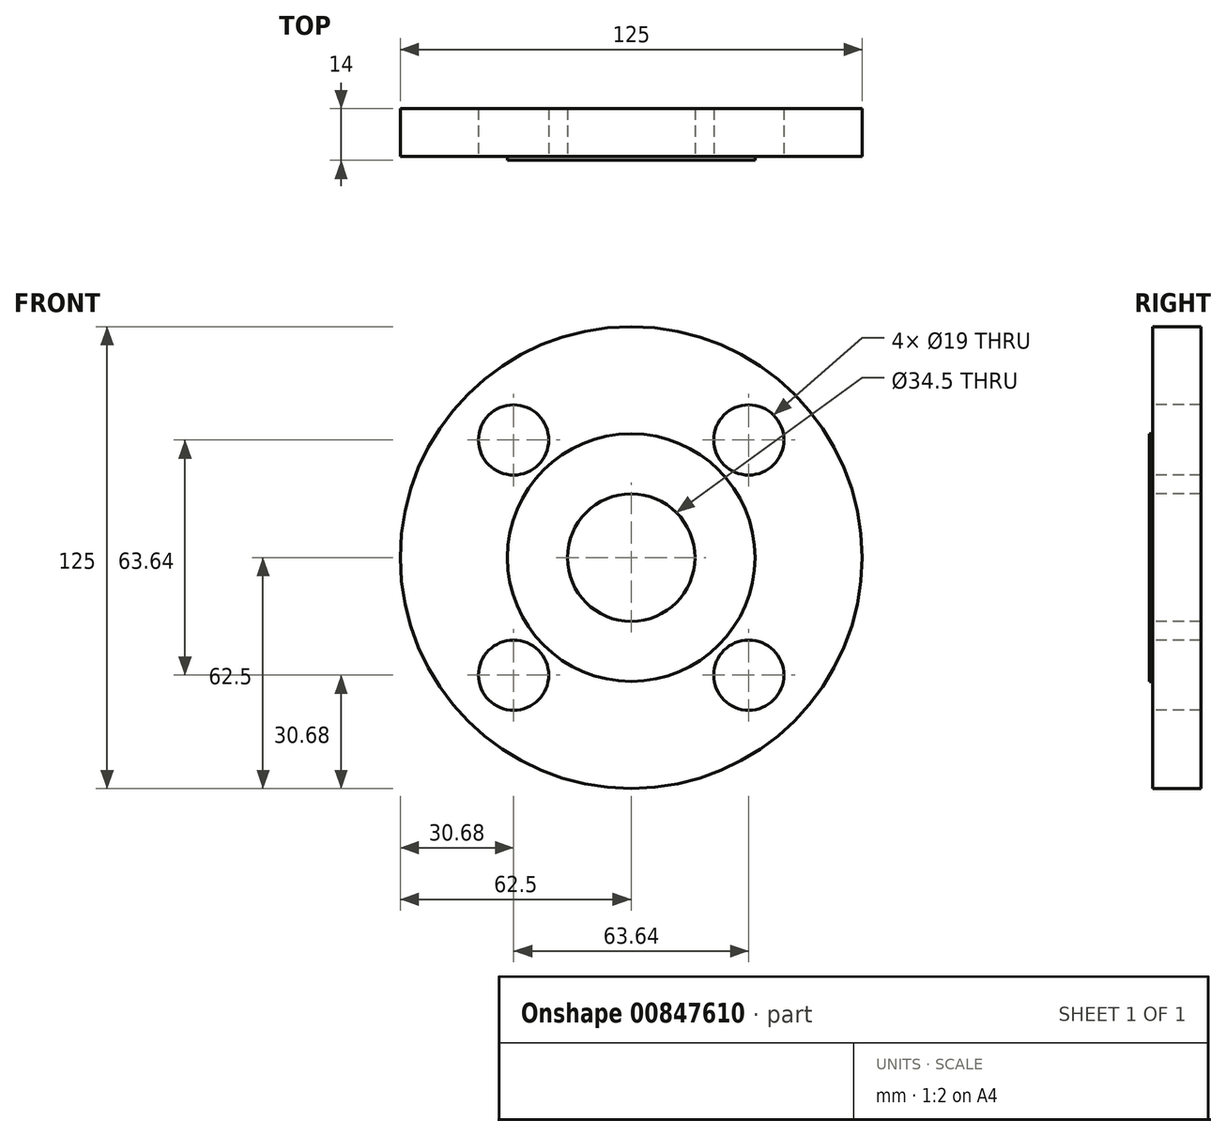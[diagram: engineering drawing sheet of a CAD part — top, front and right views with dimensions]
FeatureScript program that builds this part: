
annotation { "Feature Type Name" : "Feature", "Feature Type Description" : "" }
export const myFeature = defineFeature(function(context is Context, id is Id, definition is map)
    precondition{}
    {
        {
            var Q0;
            Q0=qCreatedBy(makeId("Front.planeOp"),FACE);
            var sketch = newSketch(context, id + "F0", { "sketchPlane" : qUnion([Q0])});
            skLineSegment(sketch, "E0", {"start": v(0, 128.5) * mm, "end": v(0, -143.3) * mm, "construction": true});
            skLineSegment(sketch, "E1", {"start": v(-175.9, 0) * mm, "end": v(185.68, 0) * mm, "construction": true});
            skCircle(sketch, "E2", {"center": v(0, 0) * mm, "radius": 62.5 * mm});
            skCircle(sketch, "E3", {"center": v(0, 0) * mm, "radius": 17.25 * mm});
            skSolve(sketch);
        }
        {
            var Q0;
            Q0=qSketchRegion(id+"F0",true);
            extrude(context, id + "F1", {"entities" : qUnion([Q0]), "oppositeDirection" : true, "depth" : 14 * mm, "offsetDistance" : 25 * mm});
        }
        {
            var Q0;
            Q0=makeQuery(id+"F1.opExtrude","CAP_FACE",FACE,{"disambiguationData":[OSD([sQuery(id+"F0.wireOp",EDGE,"E2"),sQuery(id+"F0.wireOp",EDGE,"E3")])],"isStart":true});
            var sketch = newSketch(context, id + "F2", { "sketchPlane" : qUnion([Q0])});
            skCircle(sketch, "E4", {"center": v(0, 0) * mm, "radius": 33.5 * mm});
            skCircle(sketch, "E5.0", {"center": v(0, 0) * mm, "radius": 62.5 * mm});
            skSolve(sketch);
        }
        {
            var Q0;
            Q0=qSketchRegion(id+"F2",true);
            extrude(context, id + "F3", {"entities" : qUnion([Q0]), "operationType" : NewBodyOperationType.REMOVE, "oppositeDirection" : true, "depth" : 1 * mm, "offsetDistance" : 25 * mm});
        }
        {
            var Q0;
            Q0=makeQuery(id+"F1.opExtrude","CAP_FACE",FACE,{"disambiguationData":[OSD([sQuery(id+"F0.wireOp",EDGE,"E2"),sQuery(id+"F0.wireOp",EDGE,"E3")])],"isStart":true});
            var sketch = newSketch(context, id + "F4", { "sketchPlane" : qUnion([Q0])});
            skCircle(sketch, "E6", {"center": v(0, 0) * mm, "radius": 45 * mm, "construction": true});
            skLineSegment(sketch, "E7", {"start": v(87.1, 87.1) * mm, "end": v(-90.37, -90.37) * mm, "construction": true});
            skLineSegment(sketch, "E8.MirrorCS", {"start": v(102.7, 0) * mm, "end": v(-106.73, 0) * mm, "construction": true});
            skLineSegment(sketch, "E9.MirrorCS", {"start": v(0, 103) * mm, "end": v(0, -95.38) * mm, "construction": true});
            skLineSegment(sketch, "E10.MirrorCS", {"start": v(-87.1, 87.1) * mm, "end": v(90.37, -90.37) * mm, "construction": true});
            skCircle(sketch, "E11", {"center": v(-31.82, 31.82) * mm, "radius": 9.5 * mm});
            skCircle(sketch, "E12.1.0", {"center": v(-31.82, -31.82) * mm, "radius": 9.5 * mm});
            skCircle(sketch, "E12.2.0", {"center": v(31.82, -31.82) * mm, "radius": 9.5 * mm});
            skCircle(sketch, "E12.3.0", {"center": v(31.82, 31.82) * mm, "radius": 9.5 * mm});
            skSolve(sketch);
        }
        {
            var Q0;
            Q0=qSketchRegion(id+"F4",true);
            extrude(context, id + "F5", {"entities" : qUnion([Q0]), "operationType" : NewBodyOperationType.REMOVE, "endBound" : BoundingType.THROUGH_ALL, "oppositeDirection" : true, "depth" : 25 * mm, "offsetDistance" : 25 * mm});
        }
    });
